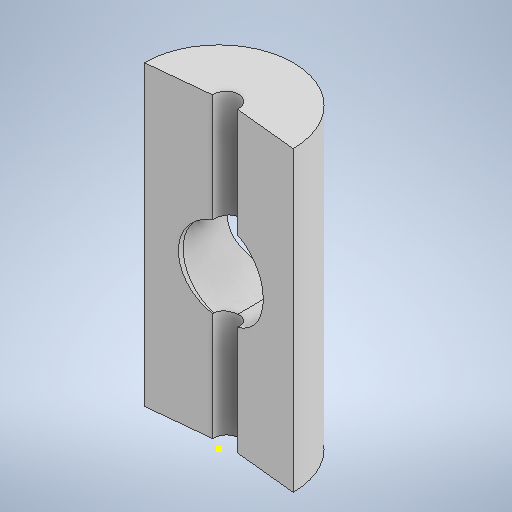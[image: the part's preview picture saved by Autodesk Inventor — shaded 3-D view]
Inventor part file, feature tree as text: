
AUTODESK INVENTOR PART (.ipt)
format: ipt  version: 2025.2 (Build 292293000, 293)  size: 260,608 bytes
history: native  units: in
note: dims shown in document units (in); Inventor stores cm internally (conversion verified against a paired STEP export)
features: sketch x6, extrude x4
ambient origin geometry x8: Origin, YZ Plane, XZ Plane, XY Plane, X Axis, Y Axis, Z Axis, Center Point
bodies: Solid1 (feature_tree)
feature tree (10):
  sketch  "Sketch1"  dims[d0=0.0591in d1=1.1811in]
  extrude  "Extrusion1"  Depth=0.0591in
  extrude  "Extrusion2"  Depth=2.3622in TaperAngle=0.0deg
  extrude  "Extrusion3"  Depth=1.378in TaperAngle=0.0deg
  extrude  "Extrusion4"  Depth=1.378in TaperAngle=0.0deg
  sketch  "Sketch6"
  sketch  "Sketch2"  dims[d2=0.1969in d3=2.3622in d4=0.0in]
  sketch  "Sketch3"  dims[d5=0.6693in d6=1.378in d7=0.0in]
  sketch  "Sketch4"  dims[d8=1.378in d9=0.0in d10=1.378in d11=0.0in]
  sketch  "Sketch5"
